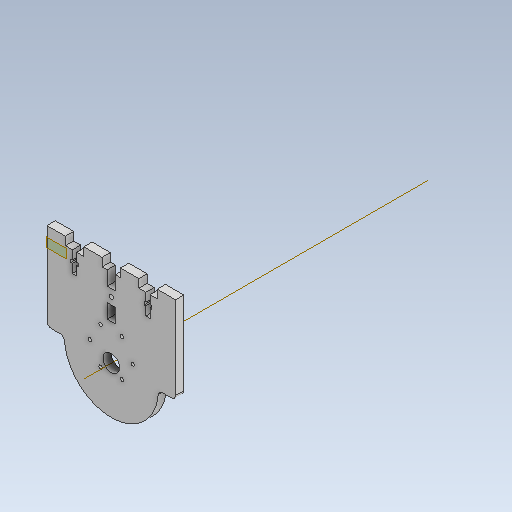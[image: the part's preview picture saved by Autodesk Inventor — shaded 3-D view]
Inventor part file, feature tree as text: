
AUTODESK INVENTOR PART (.ipt)
format: ipt  version: 2021.1 (Build 251245010, 245A)  size: 203,776 bytes
history: native  units: mm
features: other x8, reference x4, extrude x2, sketch x1
ambient origin geometry x8: Origin, YZ Plane, XZ Plane, XY Plane, X Axis, Y Axis, Z Axis, Center Point
bodies: Body1 (feature_tree)
feature tree (15):
  other  "Твердое тело1"
  other  "РабПлоскость1"
  sketch  "Эскиз1"
  other  "РабОсь1"
  extrude  "Выдавливание1"  Depth=57.0mm
  extrude  "Выдавливание2"  Depth=34.0mm
  reference  "Ссылка1"
  reference  "Ссылка2"
  reference  "Ссылка3"
  reference  "Ссылка4"
  other  "РабПлоскость2"
  other  "<userpath>\Documents\Savka\3d\Korp.iam"
  other  "Korp.iam"
  other  "Korpus 3:1"
  other  "Korpus:1"
